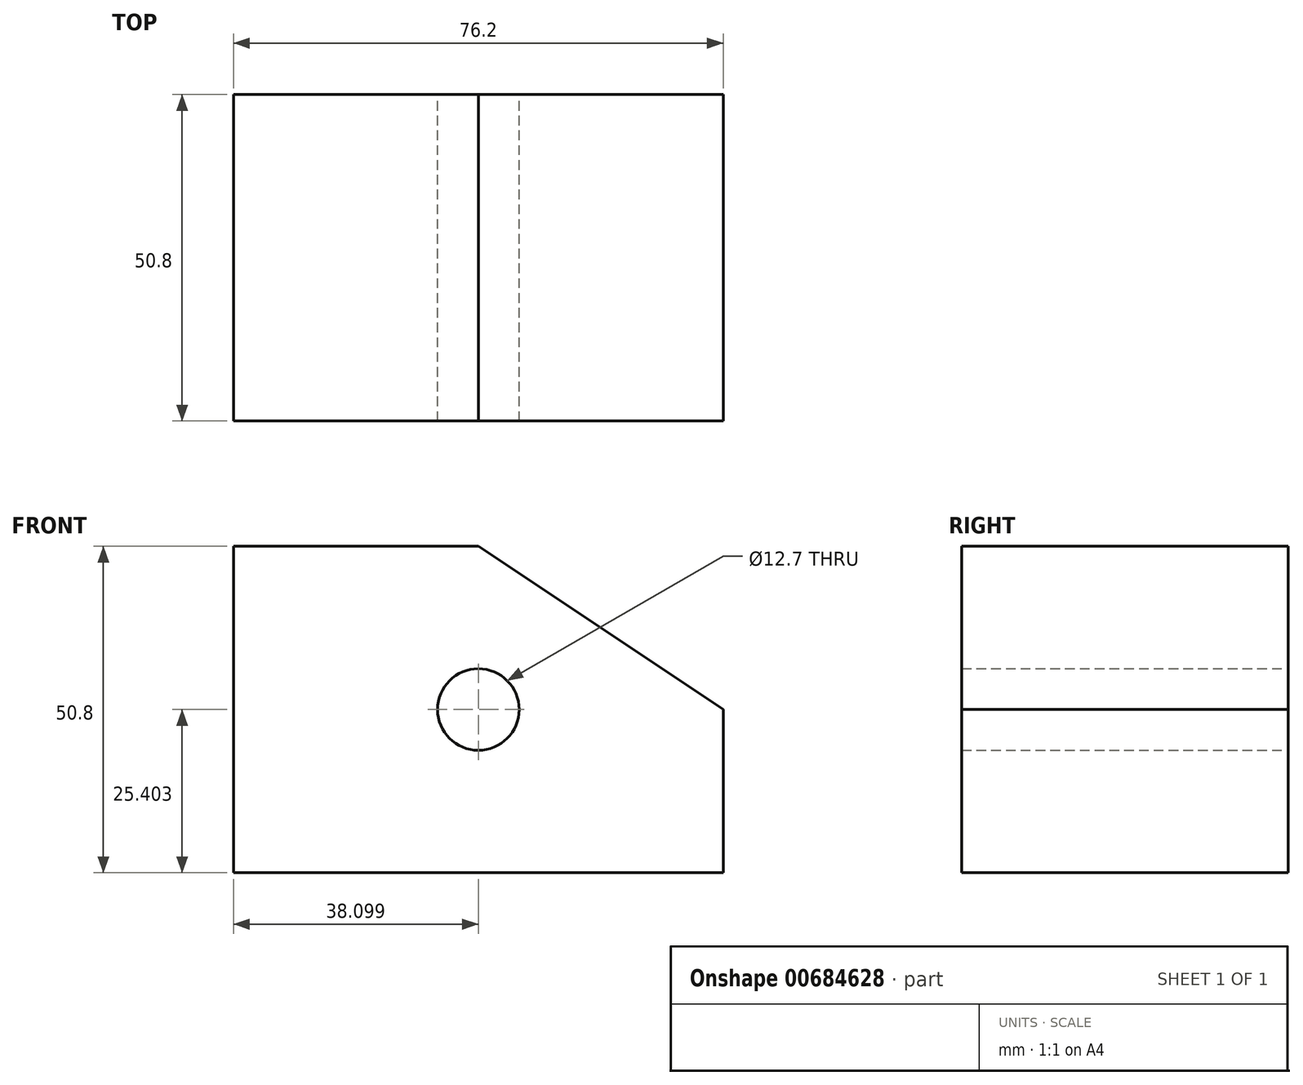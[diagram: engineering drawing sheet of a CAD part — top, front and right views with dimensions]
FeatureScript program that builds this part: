
annotation { "Feature Type Name" : "Feature", "Feature Type Description" : "" }
export const myFeature = defineFeature(function(context is Context, id is Id, definition is map)
    precondition{}
    {
        {
            var Q0;
            Q0=qCreatedBy(makeId("Front.planeOp"),FACE);
            var sketch = newSketch(context, id + "F0", { "sketchPlane" : qUnion([Q0])});
            skLineSegment(sketch, "E0", {"start": v(-60.25, 36.45) * mm, "end": v(-60.25, -14.35) * mm});
            skLineSegment(sketch, "E1", {"start": v(-60.25, -14.35) * mm, "end": v(15.95, -14.35) * mm});
            skLineSegment(sketch, "E2", {"start": v(15.95, 11.05) * mm, "end": v(15.95, -14.35) * mm});
            skLineSegment(sketch, "E3", {"start": v(-60.25, 36.45) * mm, "end": v(-22.15, 36.45) * mm});
            skLineSegment(sketch, "E4", {"start": v(-22.15, 36.45) * mm, "end": v(15.95, 11.05) * mm});
            skPoint(sketch, "E5", {"position": v(-22.15, 11.05) * mm});
            skCircle(sketch, "E6", {"center": v(-22.15, 11.05) * mm, "radius": 6.35 * mm});
            skSolve(sketch);
        }
        {
            var Q0;
            Q0 = qSketchRegion(id + "F0", true);
            extrude(context, id + "F1", {"entities" : qUnion([Q0]), "depth" : 50.8 * mm, "offsetDistance" : 25.4 * mm});
        }
    });
